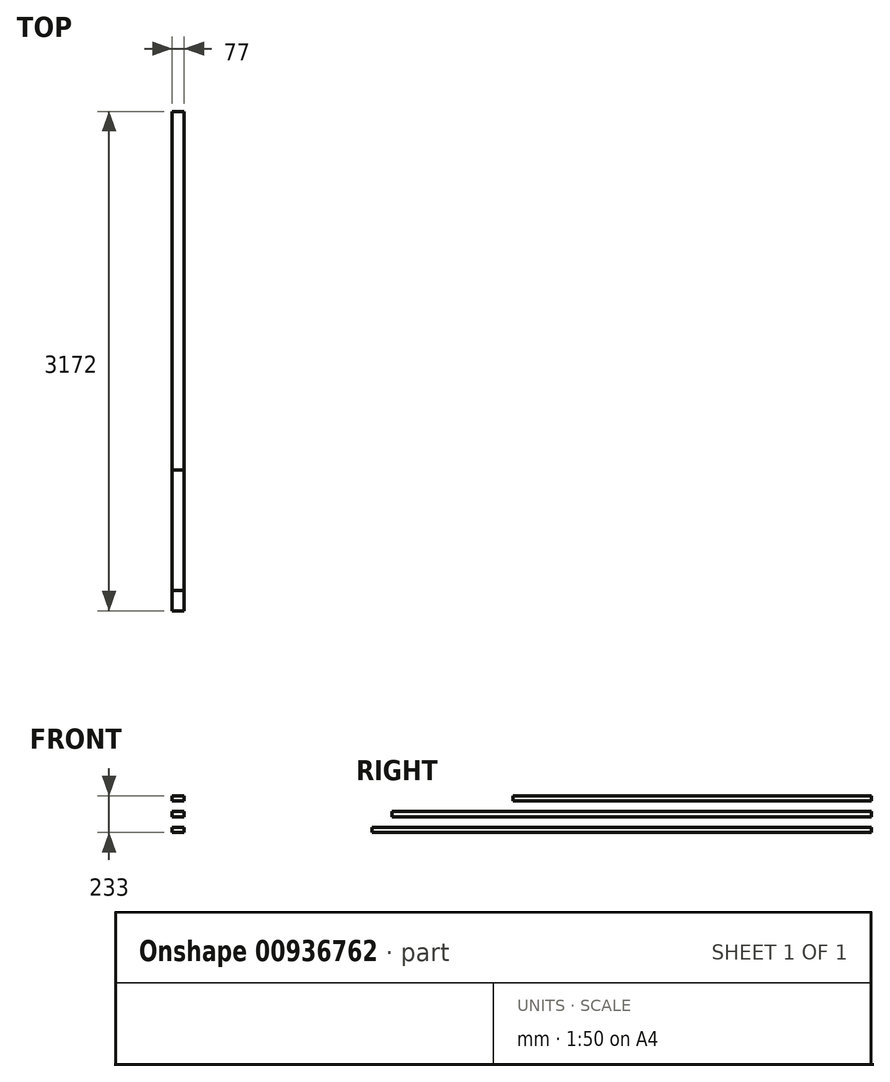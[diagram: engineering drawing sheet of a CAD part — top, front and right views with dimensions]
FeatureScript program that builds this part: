
annotation { "Feature Type Name" : "Feature", "Feature Type Description" : "" }
export const myFeature = defineFeature(function(context is Context, id is Id, definition is map)
    precondition{}
    {
        {
            var Q0;
            Q0=qCreatedBy(makeId("Front.planeOp"),FACE);
            var sketch = newSketch(context, id + "F0", { "sketchPlane" : qUnion([Q0])});
            skLineSegment(sketch, "E0.bottom", {"start": v(0, 0) * mm, "end": v(77, 0) * mm});
            skLineSegment(sketch, "E0.top", {"start": v(0, 33) * mm, "end": v(77, 33) * mm});
            skLineSegment(sketch, "E0.left", {"start": v(0, 0) * mm, "end": v(0, 33) * mm});
            skLineSegment(sketch, "E0.right", {"start": v(77, 0) * mm, "end": v(77, 33) * mm});
            skLineSegment(sketch, "E1.0.1.0", {"start": v(0, 100) * mm, "end": v(0, 133) * mm});
            skLineSegment(sketch, "E1.0.1.1", {"start": v(0, 133) * mm, "end": v(77, 133) * mm});
            skLineSegment(sketch, "E1.0.1.2", {"start": v(77, 100) * mm, "end": v(77, 133) * mm});
            skLineSegment(sketch, "E1.0.1.3", {"start": v(0, 100) * mm, "end": v(77, 100) * mm});
            skLineSegment(sketch, "E1.0.2.0", {"start": v(0, 200) * mm, "end": v(0, 233) * mm});
            skLineSegment(sketch, "E1.0.2.1", {"start": v(0, 233) * mm, "end": v(77, 233) * mm});
            skLineSegment(sketch, "E1.0.2.2", {"start": v(77, 200) * mm, "end": v(77, 233) * mm});
            skLineSegment(sketch, "E1.0.2.3", {"start": v(0, 200) * mm, "end": v(77, 200) * mm});
            skLineSegment(sketch, "E1.0.3.0", {"start": v(0, 300) * mm, "end": v(0, 333) * mm});
            skLineSegment(sketch, "E1.0.3.1", {"start": v(0, 333) * mm, "end": v(77, 333) * mm});
            skLineSegment(sketch, "E1.0.3.2", {"start": v(77, 300) * mm, "end": v(77, 333) * mm});
            skLineSegment(sketch, "E1.0.3.3", {"start": v(0, 300) * mm, "end": v(77, 300) * mm});
            skLineSegment(sketch, "E1.0.4.0", {"start": v(0, 400) * mm, "end": v(0, 433) * mm});
            skLineSegment(sketch, "E1.0.4.1", {"start": v(0, 433) * mm, "end": v(77, 433) * mm});
            skLineSegment(sketch, "E1.0.4.2", {"start": v(77, 400) * mm, "end": v(77, 433) * mm});
            skLineSegment(sketch, "E1.0.4.3", {"start": v(0, 400) * mm, "end": v(77, 400) * mm});
            skLineSegment(sketch, "E1.0.5.0", {"start": v(0, 500) * mm, "end": v(0, 533) * mm});
            skLineSegment(sketch, "E1.0.5.1", {"start": v(0, 533) * mm, "end": v(77, 533) * mm});
            skLineSegment(sketch, "E1.0.5.2", {"start": v(77, 500) * mm, "end": v(77, 533) * mm});
            skLineSegment(sketch, "E1.0.5.3", {"start": v(0, 500) * mm, "end": v(77, 500) * mm});
            skLineSegment(sketch, "E1.0.6.0", {"start": v(0, 600) * mm, "end": v(0, 633) * mm});
            skLineSegment(sketch, "E1.0.6.1", {"start": v(0, 633) * mm, "end": v(77, 633) * mm});
            skLineSegment(sketch, "E1.0.6.2", {"start": v(77, 600) * mm, "end": v(77, 633) * mm});
            skLineSegment(sketch, "E1.0.6.3", {"start": v(0, 600) * mm, "end": v(77, 600) * mm});
            skLineSegment(sketch, "E1.0.7.0", {"start": v(0, 700) * mm, "end": v(0, 733) * mm});
            skLineSegment(sketch, "E1.0.7.1", {"start": v(0, 733) * mm, "end": v(77, 733) * mm});
            skLineSegment(sketch, "E1.0.7.2", {"start": v(77, 700) * mm, "end": v(77, 733) * mm});
            skLineSegment(sketch, "E1.0.7.3", {"start": v(0, 700) * mm, "end": v(77, 700) * mm});
            skLineSegment(sketch, "E1.0.8.0", {"start": v(0, 800) * mm, "end": v(0, 833) * mm});
            skLineSegment(sketch, "E1.0.8.1", {"start": v(0, 833) * mm, "end": v(77, 833) * mm});
            skLineSegment(sketch, "E1.0.8.2", {"start": v(77, 800) * mm, "end": v(77, 833) * mm});
            skLineSegment(sketch, "E1.0.8.3", {"start": v(0, 800) * mm, "end": v(77, 800) * mm});
            skLineSegment(sketch, "E1.0.9.0", {"start": v(0, 900) * mm, "end": v(0, 933) * mm});
            skLineSegment(sketch, "E1.0.9.1", {"start": v(0, 933) * mm, "end": v(77, 933) * mm});
            skLineSegment(sketch, "E1.0.9.2", {"start": v(77, 900) * mm, "end": v(77, 933) * mm});
            skLineSegment(sketch, "E1.0.9.3", {"start": v(0, 900) * mm, "end": v(77, 900) * mm});
            skLineSegment(sketch, "E1.direction1", {"start": v(0, 0) * mm, "end": v(25, 0) * mm, "construction": true});
            skLineSegment(sketch, "E1.direction2", {"start": v(0, 0) * mm, "end": v(0, 100) * mm, "construction": true});
            skSolve(sketch);
        }
        {
            var Q0;
            Q0=makeQuery(id+"F0.imprint","IMPRINT",FACE,{"disambiguationData":[TD([[makeQuery(id+"F0.imprint","IMPRINT",EDGE,{"derivedFrom":sQuery(id+"F0.wireOp",EDGE,"E0.bottom")}),1.0]])]});
            extrude(context, id + "F1", {"entities" : qUnion([Q0]), "depth" : 3172 * mm, "offsetDistance" : 25 * mm});
        }
        {
            var Q0;
            Q0=makeQuery(id+"F0.imprint","IMPRINT",FACE,{"disambiguationData":[TD([[makeQuery(id+"F0.imprint","IMPRINT",EDGE,{"derivedFrom":sQuery(id+"F0.wireOp",EDGE,"E1.0.1.0")}),-1.0]])]});
            extrude(context, id + "F2", {"entities" : qUnion([Q0]), "depth" : 3044 * mm, "offsetDistance" : 25 * mm});
        }
        {
            var Q0;
            Q0=makeQuery(id+"F0.imprint","IMPRINT",FACE,{"disambiguationData":[TD([[makeQuery(id+"F0.imprint","IMPRINT",EDGE,{"derivedFrom":sQuery(id+"F0.wireOp",EDGE,"E1.0.2.0")}),-1.0]])]});
            extrude(context, id + "F3", {"entities" : qUnion([Q0]), "depth" : 2276 * mm, "offsetDistance" : 25 * mm});
        }
    });
